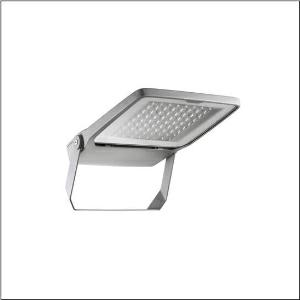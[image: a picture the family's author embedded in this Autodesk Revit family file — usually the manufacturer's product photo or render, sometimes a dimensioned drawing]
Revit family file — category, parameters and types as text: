
# Revit family: floodlight_fl_20_mini___pl52_5xa7672c2d1ac_d441
name_source: partatom
category: Lighting Fixtures
units: mm (PartAtom-declared; Revit-internal decimal feet)

## family parameters
Cut with Voids When Loaded = No
Host = Face
Light Source = No
Part Type = Normal
Room Calculation Point = No
Round Connector Dimension = Use Diameter
Shared = No

## types (1)
- --- (1 x LED 4000K / CRI = 70 (unbekannt), 12290 lm, 4000K)
    Apparent Load = 96 VA
    CIE Flux Codes = 27 59 98 100 100
    Color Rendering = 70
    Color Temperature = 4000K
    Default Elevation = 1800 mm
    Description = Floodlight FL 20 mini, floodlight, primary light control with lens, of plastic, primary optical cover: protective disc, of toughened safety glass, transparent, light distribution: PL52, light emission: direct distribution, primary light characteristic: asymmetric, installation type: surface-mounted, LED, High Power LED, rated luminous flux: 12.290lm, luminous efficacy: 128lm/W, light colour: 740, colour temperature: 4000K, control gear: ECG Plus, control: flexible luminous flux parameterisation, time-dependent luminous flux control, digital communication interface, power reduction, overheat protection, electronic power reduction, with terminal, 5-pole, max. 2.5mm², mains connection: 220..240V, AC, 50/60Hz, rated input power: 96W, LED unit, of diecast aluminium, powder-coated, Siteco® metallic grey (DB 702S), corrosivity category C5 mid according to DIN EN ISO 12944, incl. 1x M20 cable gland for cable Ø 6.5..12mm, length: 446mm, width: 355mm, height: 62mm, housing frame, of diecast aluminium, powder-coated, Siteco® metallic grey (DB 702S), mounting bracket, of steel, powder-coated, Siteco® metallic grey (DB 702S), DALI, protection rating (complete): IP66, insulation class (complete): insulation class II (safety insulation), certification: CE, ENEC, VDE, protection symbol: D, permissible operating ambient temperature: -40..+40°C, permissible operating ambient temperature for outdoor applications: -40..+50°C, standard: DIN EN 12944, packaging unit: 1 piece

Light Distribution: PL52
    Height = 62 mm  [stored 0.203412 ft]
    Lamp = 1 x LED 4000K / CRI >= 70 (unbekannt)
    Lamp Light Flux = 12290 lm
    Lamp count = 1
    Length = 467 mm
    Luminous efficacy = 128 lm/W
    Manufacturer = Siteco
    ModVariant = No
    Model = 5XA7672C2D1AC
    Mounting Place = Wall
    Mounting Type = Surface mounted
    Number of Poles = 1
    OnlyDefault = Yes
    Power Factor = 1
    Product Name = Floodlight FL 20 mini | PL52
    Product group = floodlight | wall mounted
    ProductGroupID = 2001
    Protection Class = Protection class II
    Protection Degree = IP 66
    RLX_Detail_Level = 1
    RLX_Emergency_Light_Flux = 0 lm
    RLX_Emergency_Type = 0
    RLX_Emergency_Type_DB = No
    RlxData = <blob elided: 74613 chars, md5=8df8bd73>
    Socket = socket
    Standby Power = 0 W
    System Light Flux = 12290 lm
    System Power = 96 W
    Type Comments = factory setting: luminous flux: 100 % | dim-lin: 254 | 500 mA
    Type Image = l_1005948.jpg
    URL = http://relux.com
    VarID = @adj_163885
    Voltage = 0 V
    Weight = 0.00 kg
    Width = 335 mm

note: [stored X ft] marks values corroborated as IEEE doubles in the binary element streams (Revit-internal decimal feet)

## geometry (parser evidence)
native form markers: Blend x4, Sweep x13
no freeform markers — native parametric forms only
